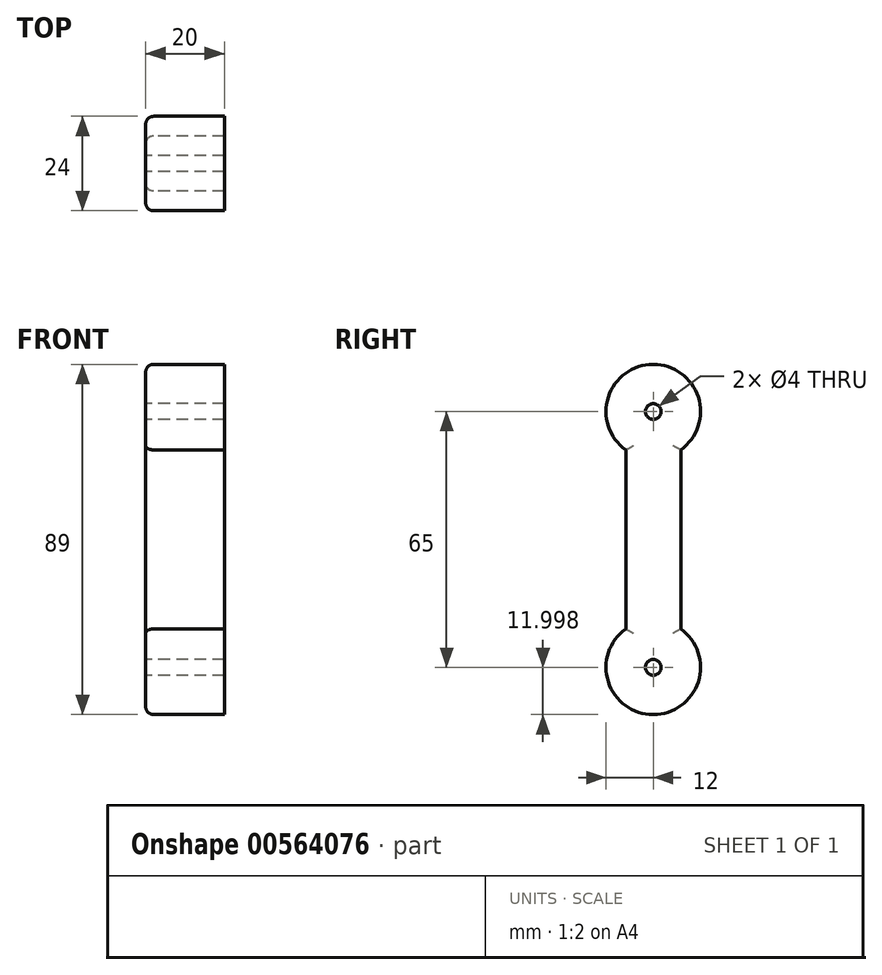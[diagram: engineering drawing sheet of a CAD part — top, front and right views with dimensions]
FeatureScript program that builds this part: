
annotation { "Feature Type Name" : "Feature", "Feature Type Description" : "" }
export const myFeature = defineFeature(function(context is Context, id is Id, definition is map)
    precondition{}
    {
        {
            var Q0;
            Q0=qCreatedBy(makeId("Right.planeOp"),FACE);
            var sketch = newSketch(context, id + "F0", { "sketchPlane" : qUnion([Q0])});
            skLineSegment(sketch, "E0", {"start": v(0, -31.23) * mm, "end": v(0, 33.77) * mm, "construction": true});
            skCircle(sketch, "E1", {"center": v(0, 33.77) * mm, "radius": 2 * mm});
            skCircle(sketch, "E2", {"center": v(0, -31.23) * mm, "radius": 2 * mm});
            skLineSegment(sketch, "E3", {"start": v(-7, 24.02) * mm, "end": v(-7, -21.48) * mm});
            skLineSegment(sketch, "E4", {"start": v(7, 24.02) * mm, "end": v(7, -21.48) * mm});
            skArc(sketch, "E5", {"start": v(-7, -21.48) * mm, "mid": v(0, -43.23) * mm, "end": v(7, -21.48) * mm});
            skArc(sketch, "E6", {"start": v(-7, 24.02) * mm, "mid": v(0, 45.77) * mm, "end": v(7, 24.02) * mm});
            skSolve(sketch);
        }
        {
            var Q0;
            Q0=makeQuery(id+"F0.imprint","IMPRINT",FACE,{"disambiguationData":[TD([[makeQuery(id+"F0.imprint","IMPRINT",EDGE,{"derivedFrom":sQuery(id+"F0.wireOp",EDGE,"E1")}),-1.0]])]});
            extrude(context, id + "F1", {"entities" : qUnion([Q0]), "depth" : 20 * mm, "offsetDistance" : 25 * mm});
        }
        {
            var Q0;
            Q0=makeQuery(id+"F1.opExtrude","CAP_EDGE",EDGE,{"disambiguationData":[OSD([sQuery(id+"F0.wireOp",EDGE,"E3")])],"isStart":true});
            var Q1;
            Q1=makeQuery(id+"F1.opExtrude","CAP_EDGE",EDGE,{"disambiguationData":[OSD([sQuery(id+"F0.wireOp",EDGE,"E5")])],"isStart":true});
            var Q2;
            Q2=makeQuery(id+"F1.opExtrude","CAP_EDGE",EDGE,{"disambiguationData":[OSD([sQuery(id+"F0.wireOp",EDGE,"E4")])],"isStart":true});
            var Q3;
            Q3=makeQuery(id+"F1.opExtrude","CAP_EDGE",EDGE,{"disambiguationData":[OSD([sQuery(id+"F0.wireOp",EDGE,"E6")])],"isStart":true});
            fillet(context, id + "F2", {"entities" : qUnion([Q0, Q1, Q2, Q3]), "radius" : 2 * mm, "tangentPropagation" : true, "allowEdgeOverflow" : false});
        }
    });
